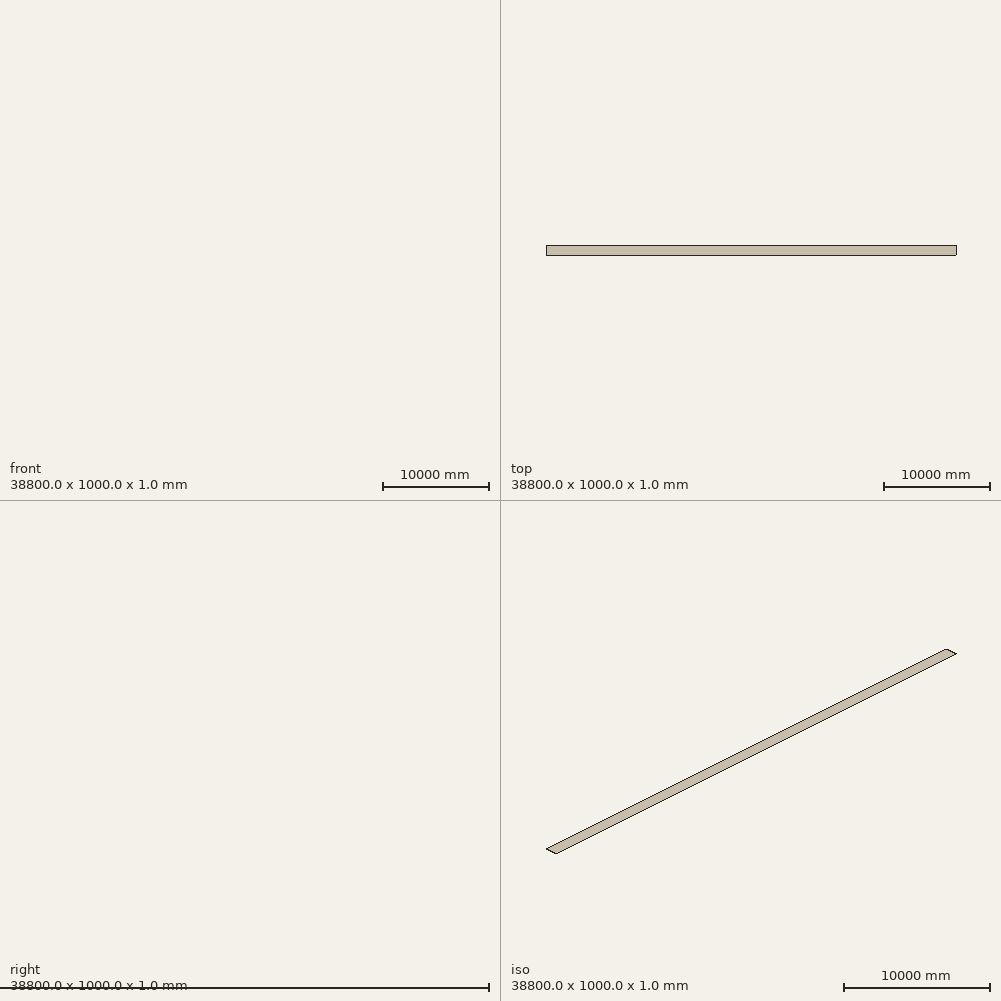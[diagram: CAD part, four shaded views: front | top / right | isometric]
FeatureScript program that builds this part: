
annotation { "Feature Type Name" : "Feature", "Feature Type Description" : "" }
export const myFeature = defineFeature(function(context is Context, id is Id, definition is map)
    precondition{}
    {
        {
            var Q0;
            Q0=qCreatedBy(makeId("Top.planeOp"),FACE);
            var sketch = newSketch(context, id + "F0", { "sketchPlane" : qUnion([Q0])});
            skLineSegment(sketch, "E0.bottom", {"start": v(0, 0) * mm, "end": v(-38800, 0) * mm});
            skLineSegment(sketch, "E0.top", {"start": v(0, -1000) * mm, "end": v(-38800, -1000) * mm});
            skLineSegment(sketch, "E0.left", {"start": v(0, 0) * mm, "end": v(0, -1000) * mm});
            skLineSegment(sketch, "E0.right", {"start": v(-38800, 0) * mm, "end": v(-38800, -1000) * mm});
            skSolve(sketch);
        }
        {
            var Q0;
            Q0 = qSketchRegion(id + "F0", true);
            extrude(context, id + "F1", {"entities" : qUnion([Q0]), "depth" : 1 * mm});
        }
    });
